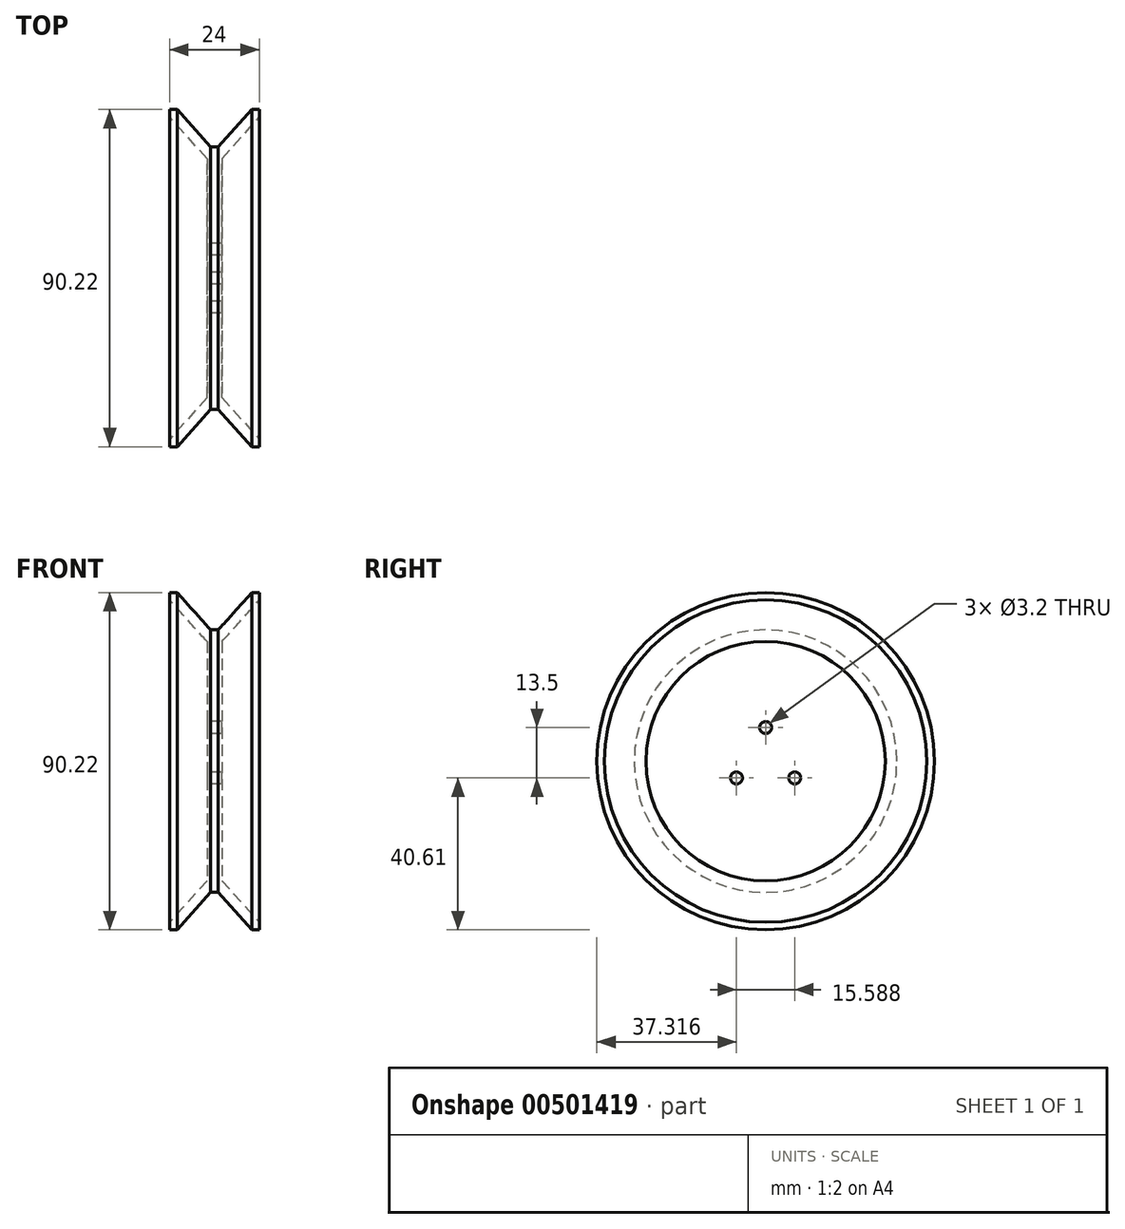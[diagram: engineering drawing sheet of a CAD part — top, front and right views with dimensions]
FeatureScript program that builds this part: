
annotation { "Feature Type Name" : "Feature", "Feature Type Description" : "" }
export const myFeature = defineFeature(function(context is Context, id is Id, definition is map)
    precondition{}
    {
        {
            var Q0;
            Q0=qCreatedBy(makeId("Front.planeOp"),FACE);
            var sketch = newSketch(context, id + "F0", { "sketchPlane" : qUnion([Q0])});
            skLineSegment(sketch, "E0", {"start": v(-12, 45.11) * mm, "end": v(-10, 45.11) * mm});
            skLineSegment(sketch, "E1", {"start": v(-10, 45.11) * mm, "end": v(-1, 35.11) * mm});
            skLineSegment(sketch, "E2", {"start": v(-1, 35.11) * mm, "end": v(1, 35.11) * mm});
            skLineSegment(sketch, "E3", {"start": v(1, 35.11) * mm, "end": v(10, 45.11) * mm});
            skLineSegment(sketch, "E4", {"start": v(10, 45.11) * mm, "end": v(12, 45.11) * mm});
            skLineSegment(sketch, "E5", {"start": v(-2, 0) * mm, "end": v(2, 0) * mm});
            skLineSegment(sketch, "E6", {"start": v(-12, 45.11) * mm, "end": v(-12, 43.11) * mm});
            skLineSegment(sketch, "E7", {"start": v(12, 45.11) * mm, "end": v(12, 43.11) * mm});
            skLineSegment(sketch, "E8", {"start": v(-12, 43.11) * mm, "end": v(-2, 32) * mm});
            skLineSegment(sketch, "E9", {"start": v(-2, 32) * mm, "end": v(-2, 0) * mm});
            skLineSegment(sketch, "E10", {"start": v(12, 43.11) * mm, "end": v(2, 32) * mm});
            skLineSegment(sketch, "E11", {"start": v(2, 32) * mm, "end": v(2, 0) * mm});
            skSolve(sketch);
        }
        {
            var Q0;
            Q0 = qSketchRegion(id + "F0", true);
            var Q1;
            Q1=sQuery(id+"F0.wireOp",EDGE,"E5");
            revolve(context, id + "F1", {"entities" : qUnion([Q0]), "axis" : qUnion([Q1]), "revolveType" : RevolveType.FULL});
        }
        {
            var Q0;
            Q0=makeQuery(id+"F1.opRevolve","SWEPT_FACE",FACE,{"disambiguationData":[OSD([sQuery(id+"F0.wireOp",EDGE,"E9")])]});
            var sketch = newSketch(context, id + "F2", { "sketchPlane" : qUnion([Q0])});
            skCircle(sketch, "E12", {"center": v(0, 0) * mm, "radius": 9 * mm, "construction": true});
            skLineSegment(sketch, "E13", {"start": v(0, 0) * mm, "end": v(0, 12.64) * mm, "construction": true});
            skPoint(sketch, "E14", {"position": v(0, 9) * mm});
            skCircle(sketch, "E15", {"center": v(0, 9) * mm, "radius": 1.6 * mm});
            skLineSegment(sketch, "E16", {"start": v(0, 0) * mm, "end": v(-10.95, -6.32) * mm, "construction": true});
            skLineSegment(sketch, "E17", {"start": v(0, 0) * mm, "end": v(9.7, -5.6) * mm, "construction": true});
            skPoint(sketch, "E18", {"position": v(7.8, -4.5) * mm});
            skPoint(sketch, "E19", {"position": v(-7.8, -4.5) * mm});
            skCircle(sketch, "E20", {"center": v(7.8, -4.5) * mm, "radius": 1.6 * mm});
            skCircle(sketch, "E21", {"center": v(-7.8, -4.5) * mm, "radius": 1.6 * mm});
            skSolve(sketch);
        }
        {
            var Q0;
            Q0=makeQuery(id+"F2.imprint","IMPRINT",FACE,{"disambiguationData":[TD([[makeQuery(id+"F2.imprint","IMPRINT",EDGE,{"derivedFrom":sQuery(id+"F2.wireOp",EDGE,"E21")}),1.0]])]});
            var Q1;
            Q1=makeQuery(id+"F2.imprint","IMPRINT",FACE,{"disambiguationData":[TD([[makeQuery(id+"F2.imprint","IMPRINT",EDGE,{"derivedFrom":sQuery(id+"F2.wireOp",EDGE,"E20")}),1.0]])]});
            var Q2;
            Q2=makeQuery(id+"F2.imprint","IMPRINT",FACE,{"disambiguationData":[TD([[makeQuery(id+"F2.imprint","IMPRINT",EDGE,{"derivedFrom":sQuery(id+"F2.wireOp",EDGE,"E15")}),1.0]])]});
            extrude(context, id + "F3", {"entities" : qUnion([Q0, Q1, Q2]), "operationType" : NewBodyOperationType.REMOVE, "endBound" : BoundingType.THROUGH_ALL, "oppositeDirection" : true, "depth" : 25 * mm});
        }
    });
